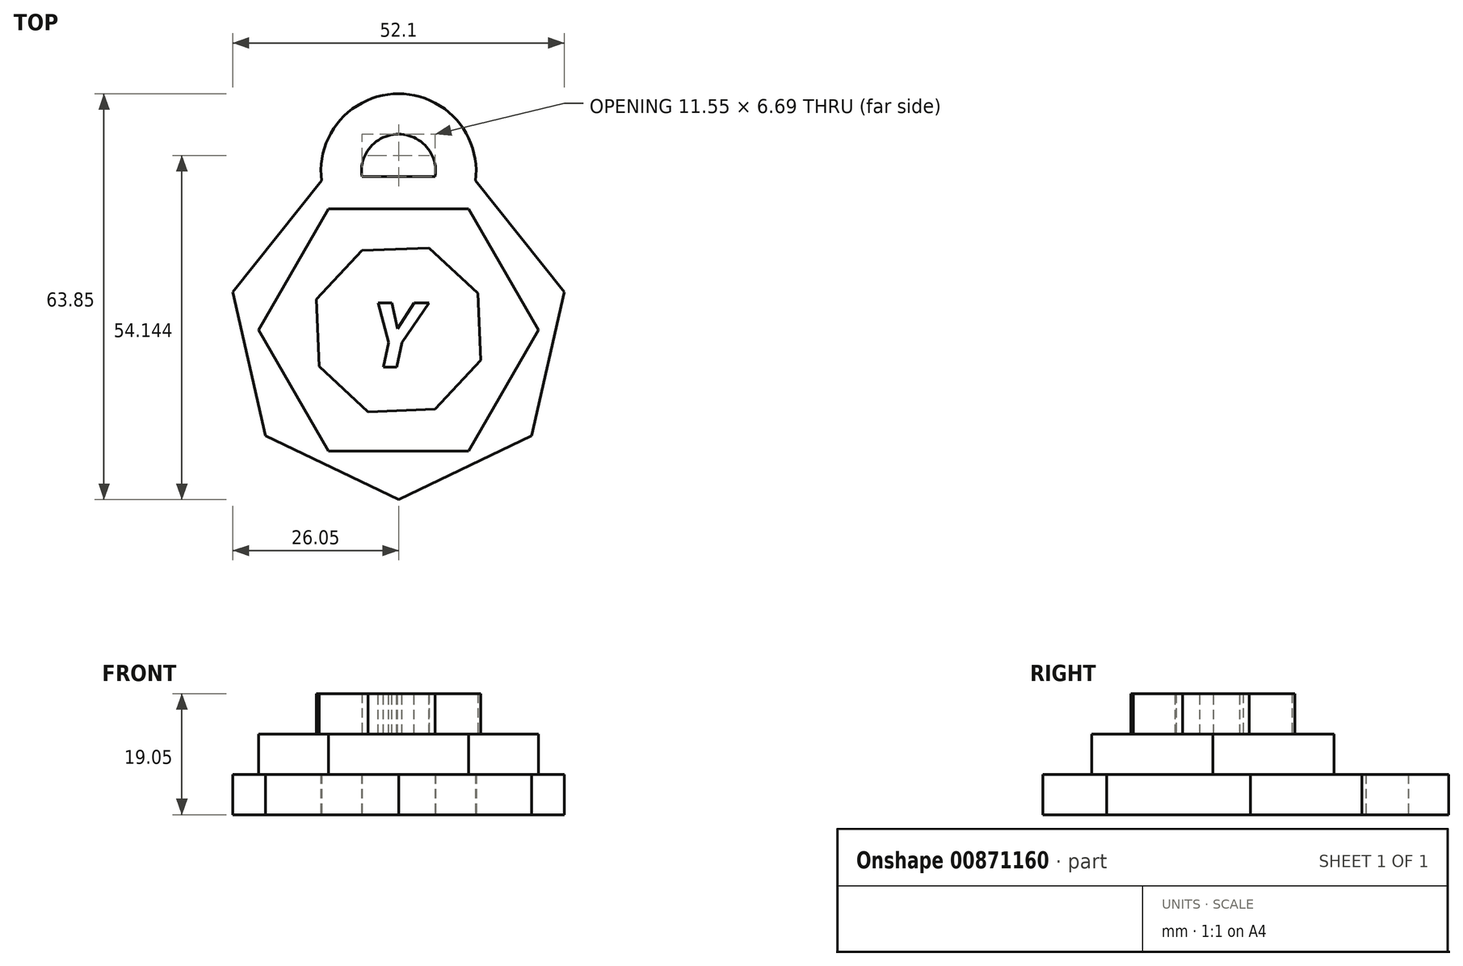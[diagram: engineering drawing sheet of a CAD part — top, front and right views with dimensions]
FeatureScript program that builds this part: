
annotation { "Feature Type Name" : "Feature", "Feature Type Description" : "" }
export const myFeature = defineFeature(function(context is Context, id is Id, definition is map)
    precondition{}
    {
        {
            var Q0;
            Q0=qCreatedBy(makeId("Top.planeOp"),FACE);
            var sketch = newSketch(context, id + "F0", { "sketchPlane" : qUnion([Q0])});
            skCircle(sketch, "E0.cCircle", {"center": v(0, 0) * mm, "radius": 24.08 * mm, "construction": true});
            skLineSegment(sketch, "E0.0", {"start": v(20.9, -16.66) * mm, "end": v(0, -26.72) * mm});
            skLineSegment(sketch, "E0.1", {"start": v(0, -26.72) * mm, "end": v(-20.9, -16.66) * mm});
            skLineSegment(sketch, "E0.2", {"start": v(-20.9, -16.66) * mm, "end": v(-26.05, 5.95) * mm});
            skLineSegment(sketch, "E0.3", {"start": v(-26.05, 5.95) * mm, "end": v(-11.6, 24.08) * mm});
            skLineSegment(sketch, "E0.4", {"start": v(-11.6, 24.08) * mm, "end": v(11.6, 24.08) * mm});
            skLineSegment(sketch, "E0.5", {"start": v(11.6, 24.08) * mm, "end": v(26.05, 5.95) * mm});
            skLineSegment(sketch, "E0.6", {"start": v(26.05, 5.95) * mm, "end": v(20.9, -16.66) * mm});
            skPoint(sketch, "E0.0.midPoint", {"position": v(10.45, -21.7) * mm});
            skSolve(sketch);
        }
        {
            var Q0;
            Q0=makeQuery(id+"F0.imprint","IMPRINT",FACE,{"disambiguationData":[TD([[makeQuery(id+"F0.imprint","IMPRINT",EDGE,{"derivedFrom":sQuery(id+"F0.wireOp",EDGE,"E0.0")}),-1.0]])]});
            extrude(context, id + "F1", {"entities" : qUnion([Q0]), "depth" : 6.35 * mm, "hasOffset" : true, "offsetDistance" : 25.4 * mm});
        }
        {
            var Q0;
            Q0=makeQuery(id+"F1.opExtrude","CAP_FACE",FACE,{"disambiguationData":[OSD([sQuery(id+"F0.wireOp",EDGE,"E0.0"),sQuery(id+"F0.wireOp",EDGE,"E0.1"),sQuery(id+"F0.wireOp",EDGE,"E0.2"),sQuery(id+"F0.wireOp",EDGE,"E0.3"),sQuery(id+"F0.wireOp",EDGE,"E0.4"),sQuery(id+"F0.wireOp",EDGE,"E0.5"),sQuery(id+"F0.wireOp",EDGE,"E0.6"),sQuery(id+"F0.wireOp",EDGE,"ea3ed94a-9c33-4ab6-91fd-df5deacde8df.0"),sQuery(id+"F0.wireOp",EDGE,"ea3ed94a-9c33-4ab6-91fd-df5deacde8df.1"),sQuery(id+"F0.wireOp",EDGE,"ea3ed94a-9c33-4ab6-91fd-df5deacde8df.2"),sQuery(id+"F0.wireOp",EDGE,"ea3ed94a-9c33-4ab6-91fd-df5deacde8df.3"),sQuery(id+"F0.wireOp",EDGE,"ea3ed94a-9c33-4ab6-91fd-df5deacde8df.4"),sQuery(id+"F0.wireOp",EDGE,"ea3ed94a-9c33-4ab6-91fd-df5deacde8df.5"),sQuery(id+"F0.wireOp",EDGE,"ea3ed94a-9c33-4ab6-91fd-df5deacde8df.6"),sQuery(id+"F0.wireOp",EDGE,"ea3ed94a-9c33-4ab6-91fd-df5deacde8df.7"),sQuery(id+"F0.wireOp",EDGE,"ea3ed94a-9c33-4ab6-91fd-df5deacde8df.8"),sQuery(id+"F0.wireOp",EDGE,"ea3ed94a-9c33-4ab6-91fd-df5deacde8df.9"),sQuery(id+"F0.wireOp",EDGE,"9069a0b1-157a-450c-8003-c642af5d630c.0"),sQuery(id+"F0.wireOp",EDGE,"9069a0b1-157a-450c-8003-c642af5d630c.1"),sQuery(id+"F0.wireOp",EDGE,"9069a0b1-157a-450c-8003-c642af5d630c.2"),sQuery(id+"F0.wireOp",EDGE,"9069a0b1-157a-450c-8003-c642af5d630c.3"),sQuery(id+"F0.wireOp",EDGE,"9069a0b1-157a-450c-8003-c642af5d630c.4"),sQuery(id+"F0.wireOp",EDGE,"9069a0b1-157a-450c-8003-c642af5d630c.5"),sQuery(id+"F0.wireOp",EDGE,"9069a0b1-157a-450c-8003-c642af5d630c.6")])],"isStart":false});
            var sketch = newSketch(context, id + "F2", { "sketchPlane" : qUnion([Q0])});
            skCircle(sketch, "E1.cCircle", {"center": v(0, 0) * mm, "radius": 19.05 * mm, "construction": true});
            skLineSegment(sketch, "E1.0", {"start": v(11, -19.05) * mm, "end": v(-11, -19.05) * mm});
            skLineSegment(sketch, "E1.1", {"start": v(-11, -19.05) * mm, "end": v(-22, 0) * mm});
            skLineSegment(sketch, "E1.2", {"start": v(-22, 0) * mm, "end": v(-11, 19.05) * mm});
            skLineSegment(sketch, "E1.3", {"start": v(-11, 19.05) * mm, "end": v(11, 19.05) * mm});
            skLineSegment(sketch, "E1.4", {"start": v(11, 19.05) * mm, "end": v(22, 0) * mm});
            skLineSegment(sketch, "E1.5", {"start": v(22, 0) * mm, "end": v(11, -19.05) * mm});
            skPoint(sketch, "E1.0.midPoint", {"position": v(0, -19.05) * mm});
            skSolve(sketch);
        }
        {
            var Q0;
            Q0=makeQuery(id+"F2.imprint","IMPRINT",FACE,{"disambiguationData":[TD([[makeQuery(id+"F2.imprint","IMPRINT",EDGE,{"derivedFrom":sQuery(id+"F2.wireOp",EDGE,"E1.0")}),-1.0]])]});
            extrude(context, id + "F3", {"entities" : qUnion([Q0]), "operationType" : NewBodyOperationType.ADD, "depth" : 6.35 * mm, "offsetDistance" : 25.4 * mm});
        }
        {
            var Q0;
            Q0=makeQuery(id+"F3.opExtrude","CAP_FACE",FACE,{"disambiguationData":[OSD([sQuery(id+"F2.wireOp",EDGE,"E1.0"),sQuery(id+"F2.wireOp",EDGE,"E1.1"),sQuery(id+"F2.wireOp",EDGE,"E1.2"),sQuery(id+"F2.wireOp",EDGE,"E1.3"),sQuery(id+"F2.wireOp",EDGE,"E1.4"),sQuery(id+"F2.wireOp",EDGE,"E1.5")])],"isStart":false});
            var sketch = newSketch(context, id + "F4", { "sketchPlane" : qUnion([Q0])});
            skCircle(sketch, "E2.cCircle", {"center": v(0, 0) * mm, "radius": 12.7 * mm, "construction": true});
            skLineSegment(sketch, "E2.0", {"start": v(12.9, -4.77) * mm, "end": v(5.74, -12.5) * mm});
            skLineSegment(sketch, "E2.1", {"start": v(5.74, -12.5) * mm, "end": v(-4.77, -12.9) * mm});
            skLineSegment(sketch, "E2.2", {"start": v(-4.77, -12.9) * mm, "end": v(-12.5, -5.74) * mm});
            skLineSegment(sketch, "E2.3", {"start": v(-12.5, -5.74) * mm, "end": v(-12.9, 4.77) * mm});
            skLineSegment(sketch, "E2.4", {"start": v(-12.9, 4.77) * mm, "end": v(-5.74, 12.5) * mm});
            skLineSegment(sketch, "E2.5", {"start": v(-5.74, 12.5) * mm, "end": v(4.77, 12.9) * mm});
            skLineSegment(sketch, "E2.6", {"start": v(4.77, 12.9) * mm, "end": v(12.5, 5.74) * mm});
            skLineSegment(sketch, "E2.7", {"start": v(12.5, 5.74) * mm, "end": v(12.9, -4.77) * mm});
            skPoint(sketch, "E2.0.midPoint", {"position": v(9.32, -8.63) * mm});
            skSolve(sketch);
        }
        {
            var Q0;
            Q0=makeQuery(id+"F4.imprint","IMPRINT",FACE,{"disambiguationData":[TD([[makeQuery(id+"F4.imprint","IMPRINT",EDGE,{"derivedFrom":sQuery(id+"F4.wireOp",EDGE,"E2.0")}),-1.0]])]});
            extrude(context, id + "F5", {"entities" : qUnion([Q0]), "operationType" : NewBodyOperationType.ADD, "depth" : 6.35 * mm, "offsetDistance" : 25.4 * mm});
        }
        {
            var Q0;
            Q0=makeQuery(id+"F5.opExtrude","CAP_FACE",FACE,{"disambiguationData":[OSD([sQuery(id+"F4.wireOp",EDGE,"E2.0"),sQuery(id+"F4.wireOp",EDGE,"E2.1"),sQuery(id+"F4.wireOp",EDGE,"E2.2"),sQuery(id+"F4.wireOp",EDGE,"E2.3"),sQuery(id+"F4.wireOp",EDGE,"E2.4"),sQuery(id+"F4.wireOp",EDGE,"E2.5"),sQuery(id+"F4.wireOp",EDGE,"E2.6"),sQuery(id+"F4.wireOp",EDGE,"E2.7")])],"isStart":false});
            var sketch = newSketch(context, id + "F6", { "sketchPlane" : qUnion([Q0])});
            skText(sketch, "E3", { "text": " Y", "fontName": "OpenSans-BoldItalic.ttf"});
            const initialGuessF6  = {"E3": [-0.00818, -0.00588, 1, 0, 0.01022]};
            skSetInitialGuess(sketch, initialGuessF6);
            skSolve(sketch);
        }
        {
            var Q0;
            Q0 = qSketchRegion(id + "F6", true);
            var Q1;
            Q1 = qConstructionFilter(qBodyType(qCreatedBy(id + "F6" ,EDGE), BodyType.WIRE), ConstructionObject.NO);
            extrude(context, id + "F7", {"entities" : qUnion([Q0]), "operationType" : NewBodyOperationType.REMOVE, "surfaceEntities" : qUnion([Q1]), "oppositeDirection" : true, "depth" : 6.35 * mm, "offsetDistance" : 25.4 * mm});
        }
        {
            var Q0;
            Q0=qCreatedBy(makeId("Top.planeOp"),FACE);
            var sketch = newSketch(context, id + "F8", { "sketchPlane" : qUnion([Q0])});
            skCircle(sketch, "E4", {"center": v(0, 24.93) * mm, "radius": 12.2 * mm});
            skCircle(sketch, "E5", {"center": v(0, 24.93) * mm, "radius": 5.84 * mm});
            skSolve(sketch);
        }
        {
            var Q0;
            Q0=makeQuery(id+"F8.imprint","IMPRINT",FACE,{"disambiguationData":[TD([[makeQuery(id+"F8.imprint","IMPRINT",EDGE,{"derivedFrom":sQuery(id+"F8.wireOp",EDGE,"E4")}),1.0]])]});
            extrude(context, id + "F9", {"entities" : qUnion([Q0]), "operationType" : NewBodyOperationType.ADD, "depth" : 6.35 * mm, "offsetDistance" : 25.4 * mm});
        }
    });
